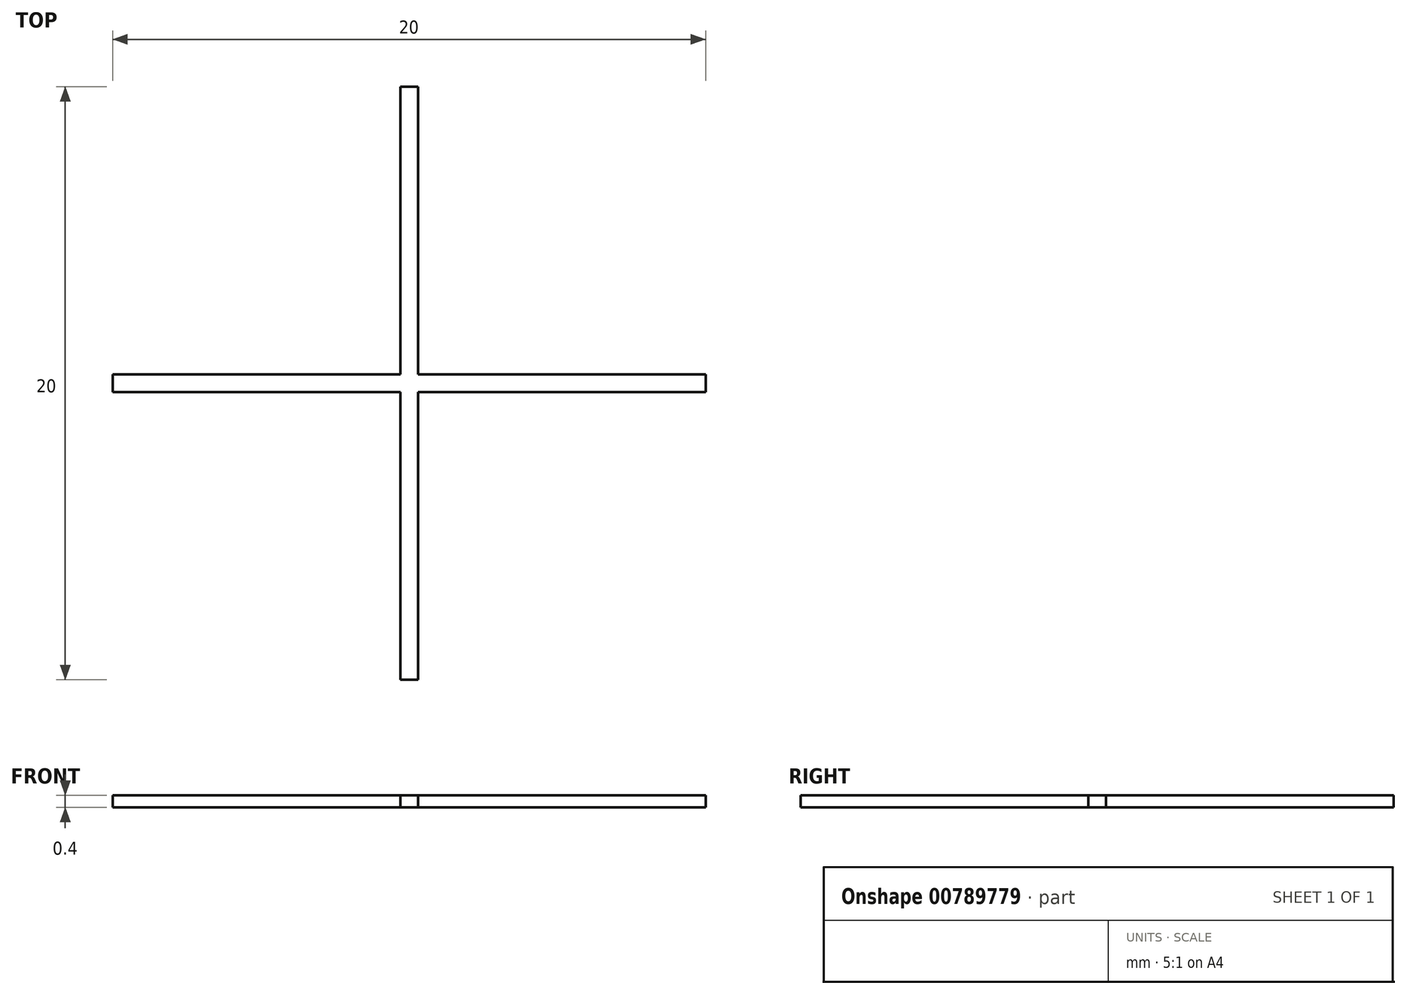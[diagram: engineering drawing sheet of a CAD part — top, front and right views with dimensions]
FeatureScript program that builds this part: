
annotation { "Feature Type Name" : "Feature", "Feature Type Description" : "" }
export const myFeature = defineFeature(function(context is Context, id is Id, definition is map)
    precondition{}
    {
        {
            var Q0;
            Q0=qCreatedBy(makeId("Top.planeOp"),FACE);
            var sketch = newSketch(context, id + "F0", { "sketchPlane" : qUnion([Q0])});
            skLineSegment(sketch, "E0.bottom", {"start": v(-0.3, 10) * mm, "end": v(0.3, 10) * mm});
            skLineSegment(sketch, "E0.top", {"start": v(-0.3, -10) * mm, "end": v(0.3, -10) * mm});
            skLineSegment(sketch, "E0.left", {"start": v(-0.3, 10) * mm, "end": v(-0.3, 0.3) * mm});
            skLineSegment(sketch, "E0.right", {"start": v(0.3, 10) * mm, "end": v(0.3, 0.3) * mm});
            skPoint(sketch, "E0.middle", {"position": v(0, 0) * mm});
            skLineSegment(sketch, "E1.1.0", {"start": v(0.3, -10) * mm, "end": v(-0.3, -10) * mm});
            skLineSegment(sketch, "E1.1.1", {"start": v(-0.3, -10) * mm, "end": v(-0.3, -0.3) * mm});
            skLineSegment(sketch, "E1.1.2", {"start": v(0.3, -10) * mm, "end": v(0.3, -0.3) * mm});
            skLineSegment(sketch, "E1.1.3", {"start": v(0.3, 10) * mm, "end": v(-0.3, 10) * mm});
            skLineSegment(sketch, "E2.1.0", {"start": v(-10, -0.3) * mm, "end": v(-0.3, -0.3) * mm});
            skLineSegment(sketch, "E2.1.1", {"start": v(-10, 0.3) * mm, "end": v(-0.3, 0.3) * mm});
            skLineSegment(sketch, "E2.1.3", {"start": v(10, -0.3) * mm, "end": v(0.3, -0.3) * mm});
            skLineSegment(sketch, "E2.1.5", {"start": v(10, 0.3) * mm, "end": v(0.3, 0.3) * mm});
            skLineSegment(sketch, "E2.1.6", {"start": v(10, -0.3) * mm, "end": v(10, 0.3) * mm});
            skLineSegment(sketch, "E2.1.7", {"start": v(-10, -0.3) * mm, "end": v(-10, 0.3) * mm});
            skLineSegment(sketch, "E2.1.8", {"start": v(10, 0.3) * mm, "end": v(10, -0.3) * mm});
            skLineSegment(sketch, "E2.1.9", {"start": v(-10, 0.3) * mm, "end": v(-10, -0.3) * mm});
            skLineSegment(sketch, "E3.trimOffspring", {"start": v(-0.3, 0.3) * mm, "end": v(-10, 0.3) * mm});
            skLineSegment(sketch, "E4.trimOffspring", {"start": v(0.3, 0.3) * mm, "end": v(10, 0.3) * mm});
            skLineSegment(sketch, "E5.trimOffspring", {"start": v(0.3, -0.3) * mm, "end": v(0.3, -10) * mm});
            skLineSegment(sketch, "E6.trimOffspring", {"start": v(-0.3, -0.3) * mm, "end": v(-10, -0.3) * mm});
            skLineSegment(sketch, "E7.trimOffspring", {"start": v(0.3, 0.3) * mm, "end": v(0.3, 10) * mm});
            skLineSegment(sketch, "E8.trimOffspring", {"start": v(-0.3, 0.3) * mm, "end": v(-0.3, 10) * mm});
            skLineSegment(sketch, "E9.trimOffspring", {"start": v(-0.3, -0.3) * mm, "end": v(-0.3, -10) * mm});
            skLineSegment(sketch, "E10.trimOffspring", {"start": v(0.3, -0.3) * mm, "end": v(10, -0.3) * mm});
            skSolve(sketch);
        }
        {
            var Q0;
            Q0 = qSketchRegion(id + "F0", true);
            extrude(context, id + "F1", {"entities" : qUnion([Q0]), "depth" : 0.4 * mm, "offsetDistance" : 25 * mm});
        }
    });
